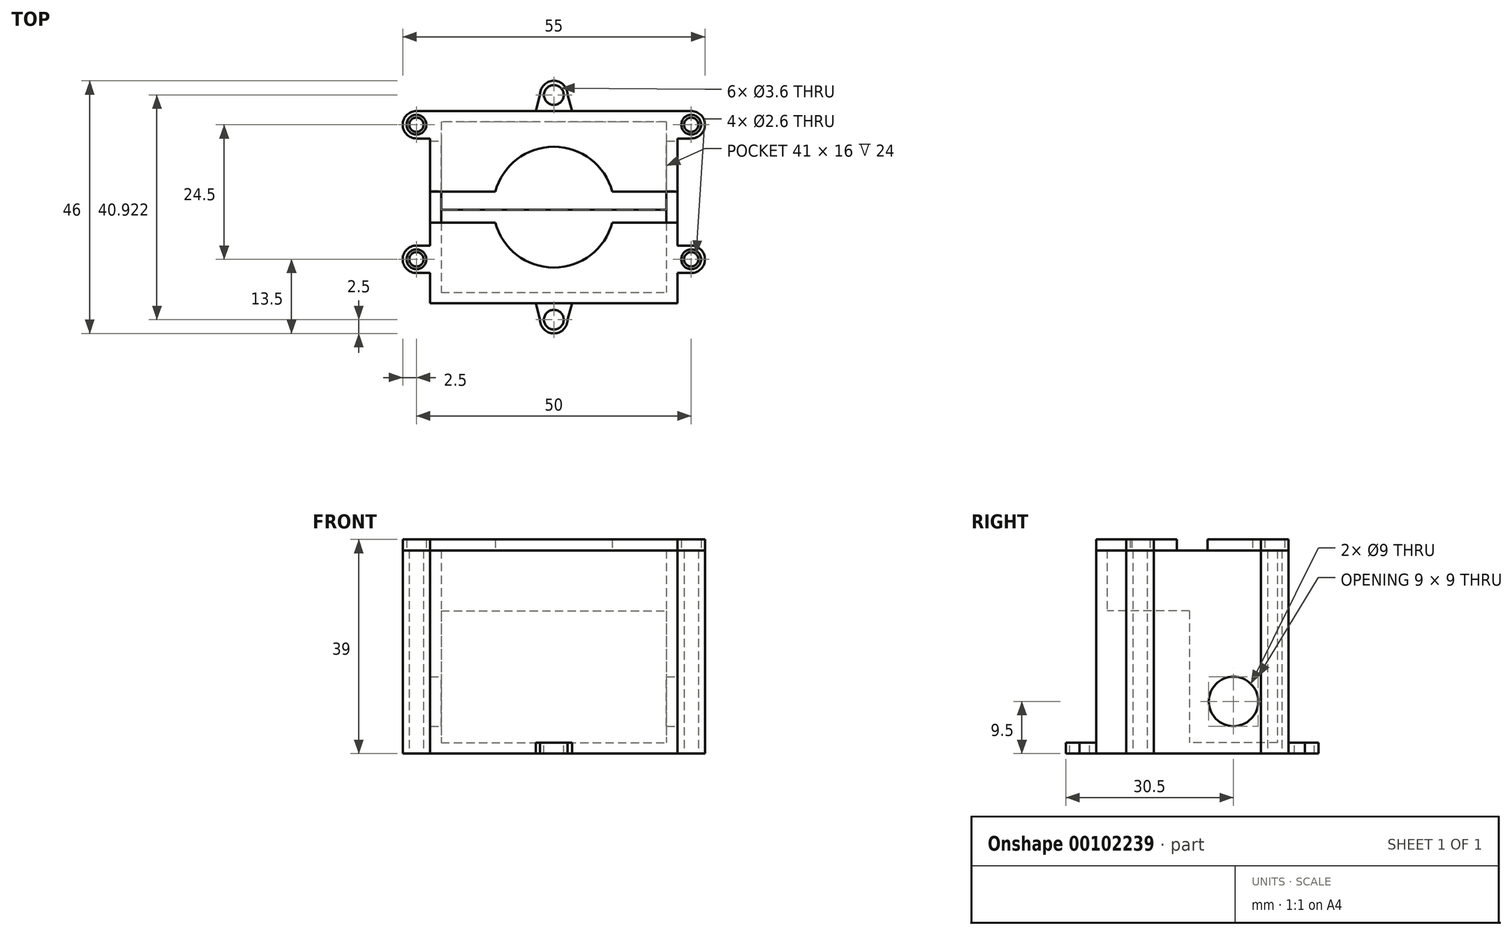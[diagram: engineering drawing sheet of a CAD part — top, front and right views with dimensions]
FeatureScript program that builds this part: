
annotation { "Feature Type Name" : "Feature", "Feature Type Description" : "" }
export const myFeature = defineFeature(function(context is Context, id is Id, definition is map)
    precondition{}
    {
        {
            var Q0;
            Q0=qCreatedBy(makeId("Top.planeOp"),FACE);
            var sketch = newSketch(context, id + "F0", { "sketchPlane" : qUnion([Q0])});
            skLineSegment(sketch, "E0.bottom", {"start": v(22.5, 17.5) * mm, "end": v(-22.5, 17.5) * mm});
            skLineSegment(sketch, "E0.top", {"start": v(22.5, -17.5) * mm, "end": v(-22.5, -17.5) * mm});
            skLineSegment(sketch, "E0.left", {"start": v(22.5, 17.5) * mm, "end": v(22.5, -17.5) * mm});
            skLineSegment(sketch, "E0.right", {"start": v(-22.5, 17.5) * mm, "end": v(-22.5, -17.5) * mm});
            skPoint(sketch, "E0.middle", {"position": v(0, 0) * mm});
            skLineSegment(sketch, "E1.bottom", {"start": v(20.5, 15.5) * mm, "end": v(-20.5, 15.5) * mm});
            skLineSegment(sketch, "E1.top", {"start": v(20.5, -15.5) * mm, "end": v(-20.5, -15.5) * mm});
            skLineSegment(sketch, "E1.left", {"start": v(20.5, 15.5) * mm, "end": v(20.5, -15.5) * mm});
            skLineSegment(sketch, "E1.right", {"start": v(-20.5, 15.5) * mm, "end": v(-20.5, -15.5) * mm});
            skSolve(sketch);
        }
        {
            var Q0;
            Q0=makeQuery(id+"F0.imprint","IMPRINT",FACE,{"disambiguationData":[TD([[makeQuery(id+"F0.imprint","IMPRINT",EDGE,{"derivedFrom":sQuery(id+"F0.wireOp",EDGE,"E0.bottom")}),1.0]])]});
            var Q1;
            Q1=makeQuery(id+"F0.imprint","IMPRINT",FACE,{"disambiguationData":[TD([[makeQuery(id+"F0.imprint","IMPRINT",EDGE,{"derivedFrom":sQuery(id+"F0.wireOp",EDGE,"E1.bottom")}),1.0]])]});
            extrude(context, id + "F1", {"entities" : qUnion([Q0, Q1]), "oppositeDirection" : true, "depth" : 2 * mm});
        }
        {
            var Q0;
            Q0=makeQuery(id+"F0.imprint","IMPRINT",FACE,{"disambiguationData":[TD([[makeQuery(id+"F0.imprint","IMPRINT",EDGE,{"derivedFrom":sQuery(id+"F0.wireOp",EDGE,"E0.bottom")}),1.0]])]});
            extrude(context, id + "F2", {"entities" : qUnion([Q0]), "operationType" : NewBodyOperationType.ADD, "depth" : 35 * mm});
        }
        {
            var Q0;
            Q0=qCreatedBy(makeId("Top.planeOp"),FACE);
            var sketch = newSketch(context, id + "F3", { "sketchPlane" : qUnion([Q0])});
            skLineSegment(sketch, "E2.bottom", {"start": v(-20.5, -0.5) * mm, "end": v(20.5, -0.5) * mm});
            skLineSegment(sketch, "E2.top", {"start": v(-20.5, -15.5) * mm, "end": v(20.5, -15.5) * mm});
            skLineSegment(sketch, "E2.left", {"start": v(-20.5, -0.5) * mm, "end": v(-20.5, -15.5) * mm});
            skLineSegment(sketch, "E2.right", {"start": v(20.5, -0.5) * mm, "end": v(20.5, -15.5) * mm});
            skSolve(sketch);
        }
        {
            var Q0;
            Q0=makeQuery(id+"F3.imprint","IMPRINT",FACE,{"disambiguationData":[TD([[makeQuery(id+"F3.imprint","IMPRINT",EDGE,{"derivedFrom":sQuery(id+"F3.wireOp",EDGE,"E2.bottom")}),-1.0]])]});
            extrude(context, id + "F4", {"entities" : qUnion([Q0]), "operationType" : NewBodyOperationType.ADD, "depth" : 24 * mm});
        }
        {
            var Q0;
            Q0=qCreatedBy(makeId("Right.planeOp"),FACE);
            var sketch = newSketch(context, id + "F5", { "sketchPlane" : qUnion([Q0])});
            skCircle(sketch, "E3", {"center": v(7.5, 7.5) * mm, "radius": 4.5 * mm});
            skSolve(sketch);
        }
        {
            var Q0;
            Q0=makeQuery(id+"F5.imprint","IMPRINT",FACE,{"disambiguationData":[TD([[makeQuery(id+"F5.imprint","IMPRINT",EDGE,{"derivedFrom":sQuery(id+"F5.wireOp",EDGE,"E3")}),1.0]])]});
            extrude(context, id + "F6", {"entities" : qUnion([Q0]), "operationType" : NewBodyOperationType.REMOVE, "endBound" : BoundingType.SYMMETRIC, "oppositeDirection" : true, "depth" : 50 * mm});
        }
        {
            var Q0;
            Q0=qCreatedBy(makeId("Top.planeOp"),FACE);
            var sketch = newSketch(context, id + "F7", { "sketchPlane" : qUnion([Q0])});
            skArc(sketch, "E4", {"start": v(2.5, 20.5) * mm, "mid": v(0, 23) * mm, "end": v(-2.5, 20.5) * mm});
            skArc(sketch, "E5", {"start": v(-2.5, -20.5) * mm, "mid": v(0, -23) * mm, "end": v(2.5, -20.5) * mm});
            skLineSegment(sketch, "E6", {"start": v(-2.5, -20.5) * mm, "end": v(-3.3, -17.5) * mm});
            skLineSegment(sketch, "E7", {"start": v(2.5, -20.5) * mm, "end": v(3.3, -17.5) * mm});
            skLineSegment(sketch, "E8", {"start": v(-3.3, -17.5) * mm, "end": v(3.3, -17.5) * mm});
            skLineSegment(sketch, "E9", {"start": v(-2.5, 20.5) * mm, "end": v(-3.3, 17.5) * mm});
            skLineSegment(sketch, "E10", {"start": v(2.5, 20.5) * mm, "end": v(3.3, 17.5) * mm});
            skLineSegment(sketch, "E11", {"start": v(-3.3, 17.5) * mm, "end": v(3.3, 17.5) * mm});
            skCircle(sketch, "E12", {"center": v(0, 20.42) * mm, "radius": 1.8 * mm});
            skLineSegment(sketch, "E13", {"start": v(-2.5, 20.5) * mm, "end": v(-2.5, 17.5) * mm, "construction": true});
            skLineSegment(sketch, "E14", {"start": v(2.5, 20.5) * mm, "end": v(2.5, 17.5) * mm, "construction": true});
            skLineSegment(sketch, "E15", {"start": v(2.5, -20.5) * mm, "end": v(2.5, -17.5) * mm, "construction": true});
            skLineSegment(sketch, "E16", {"start": v(-2.5, -20.5) * mm, "end": v(-2.5, -17.5) * mm, "construction": true});
            skLineSegment(sketch, "E17", {"start": v(-2.5, -20.5) * mm, "end": v(2.5, -20.5) * mm, "construction": true});
            skCircle(sketch, "E18", {"center": v(0, -20.5) * mm, "radius": 1.8 * mm});
            skSolve(sketch);
        }
        {
            var Q0;
            Q0=makeQuery(id+"F7.imprint","IMPRINT",FACE,{"disambiguationData":[TD([[makeQuery(id+"F7.imprint","IMPRINT",EDGE,{"derivedFrom":sQuery(id+"F7.wireOp",EDGE,"E5")}),1.0]])]});
            var Q1;
            Q1=makeQuery(id+"F7.imprint","IMPRINT",FACE,{"disambiguationData":[TD([[makeQuery(id+"F7.imprint","IMPRINT",EDGE,{"derivedFrom":sQuery(id+"F7.wireOp",EDGE,"E4")}),1.0]])]});
            extrude(context, id + "F8", {"entities" : qUnion([Q0, Q1]), "operationType" : NewBodyOperationType.ADD, "oppositeDirection" : true, "depth" : 2 * mm});
        }
        {
            var Q0;
            Q0=makeQuery(id+"F2.opExtrude","CAP_FACE",FACE,{"disambiguationData":[OSD([sQuery(id+"F0.wireOp",EDGE,"E0.bottom"),sQuery(id+"F0.wireOp",EDGE,"E0.top"),sQuery(id+"F0.wireOp",EDGE,"E0.left"),sQuery(id+"F0.wireOp",EDGE,"E0.right"),sQuery(id+"F0.wireOp",EDGE,"E1.bottom"),sQuery(id+"F0.wireOp",EDGE,"E1.top"),sQuery(id+"F0.wireOp",EDGE,"E1.left"),sQuery(id+"F0.wireOp",EDGE,"E1.right")])],"isStart":false});
            var sketch = newSketch(context, id + "F9", { "sketchPlane" : qUnion([Q0])});
            skSolve(sketch);
        }
        {
            var Q0;
            Q0=makeQuery(id+"F8.boolean.opBoolean","MERGE",FACE,{"derivedFrom":[makeQuery(id+"F1.opExtrude","CAP_FACE",FACE,{"disambiguationData":[OSD([sQuery(id+"F0.wireOp",EDGE,"E0.bottom"),sQuery(id+"F0.wireOp",EDGE,"E0.top"),sQuery(id+"F0.wireOp",EDGE,"E0.left"),sQuery(id+"F0.wireOp",EDGE,"E0.right")])],"isStart":false}),makeQuery(id+"F8.opExtrude","CAP_FACE",FACE,{"disambiguationData":[OSD([sQuery(id+"F7.wireOp",EDGE,"E4"),sQuery(id+"F7.wireOp",EDGE,"E9"),sQuery(id+"F7.wireOp",EDGE,"E10"),sQuery(id+"F7.wireOp",EDGE,"E11"),sQuery(id+"F7.wireOp",EDGE,"E12")])],"isStart":false}),makeQuery(id+"F8.opExtrude","CAP_FACE",FACE,{"disambiguationData":[OSD([sQuery(id+"F7.wireOp",EDGE,"E5"),sQuery(id+"F7.wireOp",EDGE,"E6"),sQuery(id+"F7.wireOp",EDGE,"E7"),sQuery(id+"F7.wireOp",EDGE,"E8"),sQuery(id+"F7.wireOp",EDGE,"E18")])],"isStart":false})]});
            var sketch = newSketch(context, id + "F10", { "sketchPlane" : qUnion([Q0])});
            skArc(sketch, "E19", {"start": v(-25, -12.5) * mm, "mid": v(-27.5, -15) * mm, "end": v(-25, -17.5) * mm});
            skArc(sketch, "E20", {"start": v(-25, 12) * mm, "mid": v(-27.5, 9.5) * mm, "end": v(-25, 7) * mm});
            skArc(sketch, "E21", {"start": v(25, 7) * mm, "mid": v(27.5, 9.5) * mm, "end": v(25, 12) * mm});
            skArc(sketch, "E22", {"start": v(25, -17.5) * mm, "mid": v(27.5, -15) * mm, "end": v(25, -12.5) * mm});
            skCircle(sketch, "E23", {"center": v(-25, -15) * mm, "radius": 1.3 * mm});
            skCircle(sketch, "E24", {"center": v(25, -15) * mm, "radius": 1.3 * mm});
            skCircle(sketch, "E25", {"center": v(25, 9.5) * mm, "radius": 1.3 * mm});
            skCircle(sketch, "E26", {"center": v(-25, 9.5) * mm, "radius": 1.3 * mm});
            skLineSegment(sketch, "E27", {"start": v(-25, -17.5) * mm, "end": v(-22.5, -17.5) * mm});
            skLineSegment(sketch, "E28", {"start": v(-25, -12.5) * mm, "end": v(-22.5, -12.5) * mm});
            skLineSegment(sketch, "E29", {"start": v(-25, 7) * mm, "end": v(-22.5, 7) * mm});
            skLineSegment(sketch, "E30", {"start": v(-25, 12) * mm, "end": v(-22.5, 12) * mm});
            skLineSegment(sketch, "E31", {"start": v(25, 7) * mm, "end": v(22.5, 7) * mm});
            skLineSegment(sketch, "E32", {"start": v(25, 12) * mm, "end": v(22.5, 12) * mm});
            skLineSegment(sketch, "E33", {"start": v(25, -12.5) * mm, "end": v(22.5, -12.5) * mm});
            skLineSegment(sketch, "E34", {"start": v(25, -17.5) * mm, "end": v(22.5, -17.5) * mm});
            skSolve(sketch);
        }
        {
            var Q0;
            Q0=makeQuery(id+"F10.imprint","IMPRINT",FACE,{"disambiguationData":[TD([[makeQuery(id+"F10.imprint","IMPRINT",EDGE,{"derivedFrom":sQuery(id+"F10.wireOp",EDGE,"E19")}),1.0]])]});
            var Q1;
            Q1=makeQuery(id+"F10.imprint","IMPRINT",FACE,{"disambiguationData":[TD([[makeQuery(id+"F10.imprint","IMPRINT",EDGE,{"derivedFrom":sQuery(id+"F10.wireOp",EDGE,"E22")}),1.0]])]});
            var Q2;
            Q2=makeQuery(id+"F10.imprint","IMPRINT",FACE,{"disambiguationData":[TD([[makeQuery(id+"F10.imprint","IMPRINT",EDGE,{"derivedFrom":sQuery(id+"F10.wireOp",EDGE,"E21")}),1.0]])]});
            var Q3;
            Q3=makeQuery(id+"F10.imprint","IMPRINT",FACE,{"disambiguationData":[TD([[makeQuery(id+"F10.imprint","IMPRINT",EDGE,{"derivedFrom":sQuery(id+"F10.wireOp",EDGE,"E20")}),1.0]])]});
            var Q4;
            Q4=makeQuery(id+"F2.opExtrude","CAP_FACE",FACE,{"disambiguationData":[OSD([sQuery(id+"F0.wireOp",EDGE,"E0.bottom"),sQuery(id+"F0.wireOp",EDGE,"E0.top"),sQuery(id+"F0.wireOp",EDGE,"E0.left"),sQuery(id+"F0.wireOp",EDGE,"E0.right"),sQuery(id+"F0.wireOp",EDGE,"E1.bottom"),sQuery(id+"F0.wireOp",EDGE,"E1.top"),sQuery(id+"F0.wireOp",EDGE,"E1.left"),sQuery(id+"F0.wireOp",EDGE,"E1.right")])],"isStart":false});
            extrude(context, id + "F11", {"entities" : qUnion([Q0, Q1, Q2, Q3]), "operationType" : NewBodyOperationType.ADD, "endBound" : BoundingType.UP_TO_SURFACE, "oppositeDirection" : true, "endBoundEntityFace" : qUnion([Q4]), "depth" : 10 * mm});
        }
        {
            var Q0;
            Q0=makeQuery(id+"F9.imprint","IMPRINT",FACE,{"disambiguationData":[TD([[makeQuery(id+"F9.imprint","IMPRINT",EDGE,{"derivedFrom":makeQuery(id+"F2.opExtrude","CAP_EDGE",EDGE,{"disambiguationData":[OSD([sQuery(id+"F0.wireOp",EDGE,"E0.bottom")])],"isStart":false})}),1.0]])]});
            var sketch = newSketch(context, id + "F12", { "sketchPlane" : qUnion([Q0])});
            skLineSegment(sketch, "E35.bottom", {"start": v(-22.5, -17.5) * mm, "end": v(22.5, -17.5) * mm});
            skLineSegment(sketch, "E35.top", {"start": v(-22.5, 17.5) * mm, "end": v(22.5, 17.5) * mm});
            skLineSegment(sketch, "E35.left", {"start": v(-22.5, -17.5) * mm, "end": v(-22.5, -2.8) * mm});
            skLineSegment(sketch, "E35.right", {"start": v(22.5, -17.5) * mm, "end": v(22.5, -2.8) * mm});
            skLineSegment(sketch, "E36", {"start": v(-22.5, 0) * mm, "end": v(22.5, 0) * mm, "construction": true});
            skLineSegment(sketch, "E37", {"start": v(-22.5, 2.8) * mm, "end": v(-10.64, 2.8) * mm});
            skLineSegment(sketch, "E38", {"start": v(-22.5, -2.8) * mm, "end": v(-10.64, -2.8) * mm});
            skLineSegment(sketch, "E39.trimOffspring", {"start": v(-22.5, 2.8) * mm, "end": v(-22.5, 17.5) * mm});
            skLineSegment(sketch, "E40.trimOffspring", {"start": v(22.5, 2.8) * mm, "end": v(22.5, 17.5) * mm});
            skCircle(sketch, "E41", {"center": v(0, 0) * mm, "radius": 11 * mm});
            skLineSegment(sketch, "E42.trimOffspring", {"start": v(10.64, 2.8) * mm, "end": v(22.5, 2.8) * mm});
            skLineSegment(sketch, "E43.trimOffspring", {"start": v(10.64, -2.8) * mm, "end": v(22.5, -2.8) * mm});
            skCircle(sketch, "E44", {"center": v(-25, 15) * mm, "radius": 1.8 * mm});
            skArc(sketch, "E45", {"start": v(-25, 17.5) * mm, "mid": v(-27.5, 15) * mm, "end": v(-25, 12.5) * mm});
            skLineSegment(sketch, "E46", {"start": v(-25, 17.5) * mm, "end": v(-22.5, 17.5) * mm});
            skLineSegment(sketch, "E47", {"start": v(-25, 12.5) * mm, "end": v(-22.5, 12.5) * mm});
            skCircle(sketch, "E48", {"center": v(-25, -9.5) * mm, "radius": 1.8 * mm});
            skArc(sketch, "E49", {"start": v(-25, -7) * mm, "mid": v(-27.5, -9.5) * mm, "end": v(-25, -12) * mm});
            skLineSegment(sketch, "E50", {"start": v(-25, -7) * mm, "end": v(-22.5, -7) * mm});
            skLineSegment(sketch, "E51", {"start": v(-25, -12) * mm, "end": v(-22.5, -12) * mm});
            skArc(sketch, "E52", {"start": v(25, -12) * mm, "mid": v(27.5, -9.5) * mm, "end": v(25, -7) * mm});
            skCircle(sketch, "E53", {"center": v(25, -9.5) * mm, "radius": 1.8 * mm});
            skLineSegment(sketch, "E54", {"start": v(25, -7) * mm, "end": v(22.5, -7) * mm});
            skLineSegment(sketch, "E55", {"start": v(25, -12) * mm, "end": v(22.5, -12) * mm});
            skCircle(sketch, "E56", {"center": v(25, 15) * mm, "radius": 1.8 * mm});
            skArc(sketch, "E57", {"start": v(25, 12.5) * mm, "mid": v(27.5, 15) * mm, "end": v(25, 17.5) * mm});
            skLineSegment(sketch, "E58", {"start": v(25, 17.5) * mm, "end": v(22.5, 17.5) * mm});
            skLineSegment(sketch, "E59", {"start": v(25, 12.5) * mm, "end": v(22.5, 12.5) * mm});
            skSolve(sketch);
        }
        {
            var Q0;
            Q0=makeQuery(id+"F12.imprint","IMPRINT",FACE,{"disambiguationData":[TD([[makeQuery(id+"F12.imprint","IMPRINT",EDGE,{"derivedFrom":sQuery(id+"F12.wireOp",EDGE,"E44")}),-1.0]])]});
            var Q1;
            {var subQ4=sQuery(id+"F12.wireOp",EDGE,"E35.top");Q1=makeQuery(id+"F12.imprint","IMPRINT",FACE,{"disambiguationData":[TD([[makeQuery(id+"F12.imprint","IMPRINT",EDGE,{"derivedFrom":subQ4}),1.0]])]});}
            var Q2;
            {var subQ0=makeQuery(id+"F9.imprint","IMPRINT",EDGE,{"derivedFrom":makeQuery(id+"F2.opExtrude","CAP_EDGE",EDGE,{"disambiguationData":[OSD([sQuery(id+"F0.wireOp",EDGE,"E1.bottom")])],"isStart":false})});Q2=makeQuery(id+"F12.imprint","IMPRINT",FACE,{"disambiguationData":[TD([[makeQuery(id+"F12.imprint","IMPRINT",EDGE,{"derivedFrom":subQ0}),1.0]])]});}
            var Q3;
            Q3=makeQuery(id+"F12.imprint","IMPRINT",FACE,{"disambiguationData":[TD([[makeQuery(id+"F12.imprint","IMPRINT",EDGE,{"derivedFrom":sQuery(id+"F12.wireOp",EDGE,"E56")}),-1.0]])]});
            extrude(context, id + "F13", {"entities" : qUnion([Q0, Q1, Q2, Q3]), "depth" : 2 * mm});
        }
        {
            var Q0;
            {var subQ0=makeQuery(id+"F9.imprint","IMPRINT",EDGE,{"derivedFrom":makeQuery(id+"F2.opExtrude","CAP_EDGE",EDGE,{"disambiguationData":[OSD([sQuery(id+"F0.wireOp",EDGE,"E1.top")])],"isStart":false})});Q0=makeQuery(id+"F12.imprint","IMPRINT",FACE,{"disambiguationData":[TD([[makeQuery(id+"F12.imprint","IMPRINT",EDGE,{"derivedFrom":subQ0}),-1.0]])]});}
            var Q1;
            {var subQ5=sQuery(id+"F12.wireOp",EDGE,"E35.bottom");Q1=makeQuery(id+"F12.imprint","IMPRINT",FACE,{"disambiguationData":[TD([[makeQuery(id+"F12.imprint","IMPRINT",EDGE,{"derivedFrom":subQ5}),-1.0]])]});}
            var Q2;
            Q2=makeQuery(id+"F12.imprint","IMPRINT",FACE,{"disambiguationData":[TD([[makeQuery(id+"F12.imprint","IMPRINT",EDGE,{"derivedFrom":sQuery(id+"F12.wireOp",EDGE,"E48")}),-1.0]])]});
            var Q3;
            Q3=makeQuery(id+"F12.imprint","IMPRINT",FACE,{"disambiguationData":[TD([[makeQuery(id+"F12.imprint","IMPRINT",EDGE,{"derivedFrom":sQuery(id+"F12.wireOp",EDGE,"E52")}),1.0]])]});
            extrude(context, id + "F14", {"entities" : qUnion([Q0, Q1, Q2, Q3]), "depth" : 2 * mm});
        }
    });
